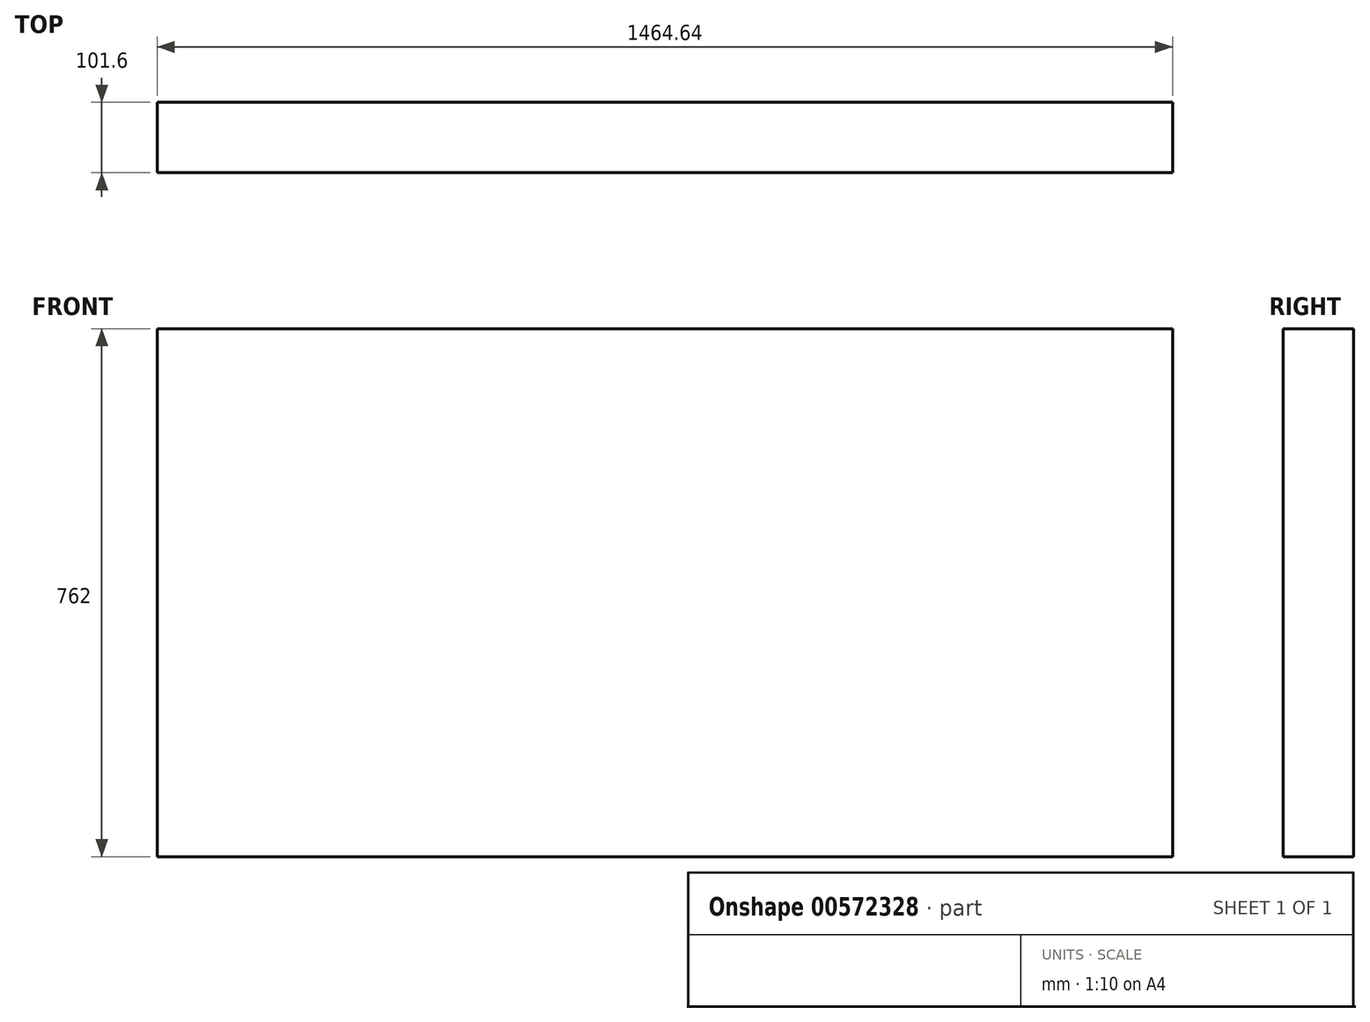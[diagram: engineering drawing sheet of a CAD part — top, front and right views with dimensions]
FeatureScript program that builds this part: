
annotation { "Feature Type Name" : "Feature", "Feature Type Description" : "" }
export const myFeature = defineFeature(function(context is Context, id is Id, definition is map)
    precondition{}
    {
        {
            var Q0;
            Q0=qCreatedBy(makeId("Front.planeOp"),FACE);
            var sketch = newSketch(context, id + "F0", { "sketchPlane" : qUnion([Q0])});
            skLineSegment(sketch, "E0.bottom", {"start": v(0, 0) * mm, "end": v(-1464.64, 0) * mm});
            skLineSegment(sketch, "E0.top", {"start": v(0, 762) * mm, "end": v(-1464.64, 762) * mm});
            skLineSegment(sketch, "E0.left", {"start": v(0, 0) * mm, "end": v(0, 762) * mm});
            skLineSegment(sketch, "E0.right", {"start": v(-1464.64, 0) * mm, "end": v(-1464.64, 762) * mm});
            skSolve(sketch);
        }
        {
            var Q0;
            Q0 = qSketchRegion(id + "F0", true);
            extrude(context, id + "F1", {"entities" : qUnion([Q0]), "depth" : 101.6 * mm, "offsetDistance" : 25.4 * mm});
        }
    });
